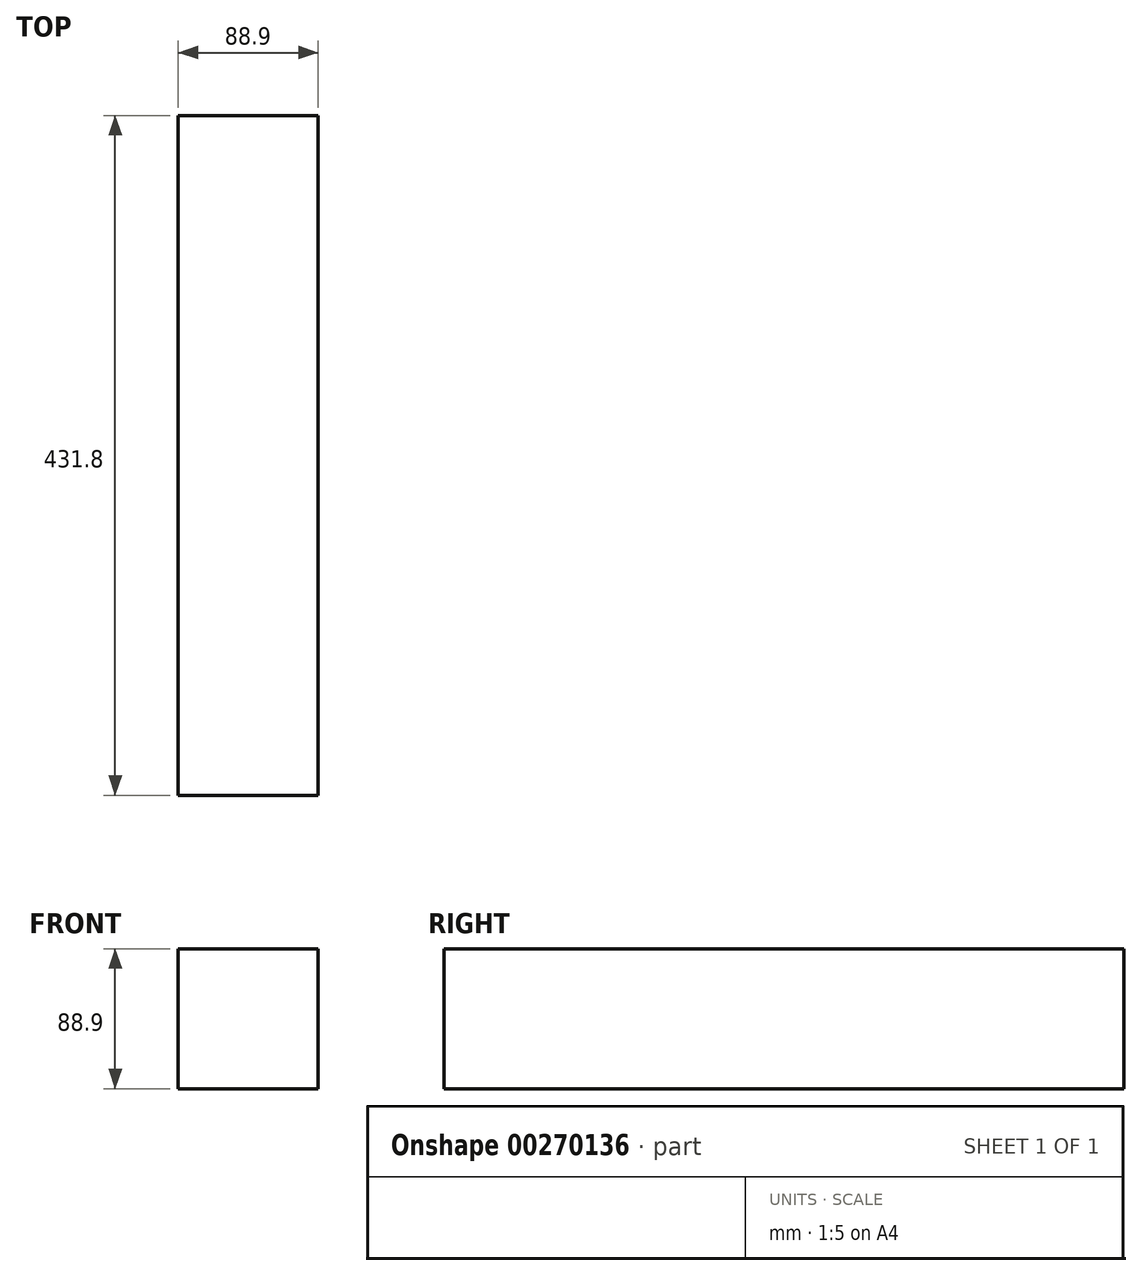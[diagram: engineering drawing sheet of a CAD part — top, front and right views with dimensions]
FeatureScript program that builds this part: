
annotation { "Feature Type Name" : "Feature", "Feature Type Description" : "" }
export const myFeature = defineFeature(function(context is Context, id is Id, definition is map)
    precondition{}
    {
        {
            var Q0;
            Q0=qCreatedBy(makeId("Front.planeOp"),FACE);
            var sketch = newSketch(context, id + "F0", { "sketchPlane" : qUnion([Q0])});
            skLineSegment(sketch, "E0.bottom", {"start": v(44.45, -44.45) * mm, "end": v(-44.45, -44.45) * mm});
            skLineSegment(sketch, "E0.top", {"start": v(44.45, 44.45) * mm, "end": v(-44.45, 44.45) * mm});
            skLineSegment(sketch, "E0.left", {"start": v(44.45, -44.45) * mm, "end": v(44.45, 44.45) * mm});
            skLineSegment(sketch, "E0.right", {"start": v(-44.45, -44.45) * mm, "end": v(-44.45, 44.45) * mm});
            skPoint(sketch, "E0.middle", {"position": v(0, 0) * mm});
            skSolve(sketch);
        }
        {
            var Q0;
            Q0=makeQuery(id+"F0.imprint","IMPRINT",FACE,{"disambiguationData":[TD([[makeQuery(id+"F0.imprint","IMPRINT",EDGE,{"derivedFrom":sQuery(id+"F0.wireOp",EDGE,"E0.bottom")}),-1.0]])]});
            extrude(context, id + "F1", {"entities" : qUnion([Q0]), "depth" : 431.8 * mm});
        }
    });
